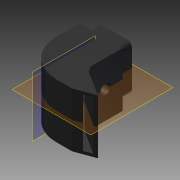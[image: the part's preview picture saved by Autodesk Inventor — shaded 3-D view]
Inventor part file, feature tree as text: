
AUTODESK INVENTOR PART (.ipt)
format: ipt  version: 2015 (Build 190159000, 159)  size: 222,720 bytes
history: native  units: mm
features: extrude x7, hole x2, shell x1, plane x1, fillet x1, other x1
ambient origin geometry x8: Origin, YZ Plane, XZ Plane, XY Plane, X Axis, Y Axis, Z Axis, Center Point
bodies: Solid1 (feature_tree)
feature tree (13):
  extrude  "Extrusión1"  Depth=15.0mm
  hole  "Agujero1"  [1 undecoded]
  shell  "Vaciado1"  Thickness=21.0mm
  plane  "Plano de trabajo2"
  extrude  "Extrusión17"  Depth=19.0mm TaperAngle=0.0deg
  hole  "Agujero4"  [1 undecoded]
  extrude  "Extrusión18"  Depth=6.0mm
  extrude  "Extrusión19"  Depth=1.0mm
  extrude  "Extrusión20"  Depth=3.0mm
  extrude  "Extrusión21"  Depth=3.0mm
  fillet  "Empalme8"  Radius=10.0mm
  other  "Desplazar cara4"
  extrude  "Extrusión22"  Depth=4.0mm
note: 2 required parameter values undecoded (feature->parameter linkage not recoverable at this tier; creation-order binding heuristic only, values carry confidence <= 0.55)
